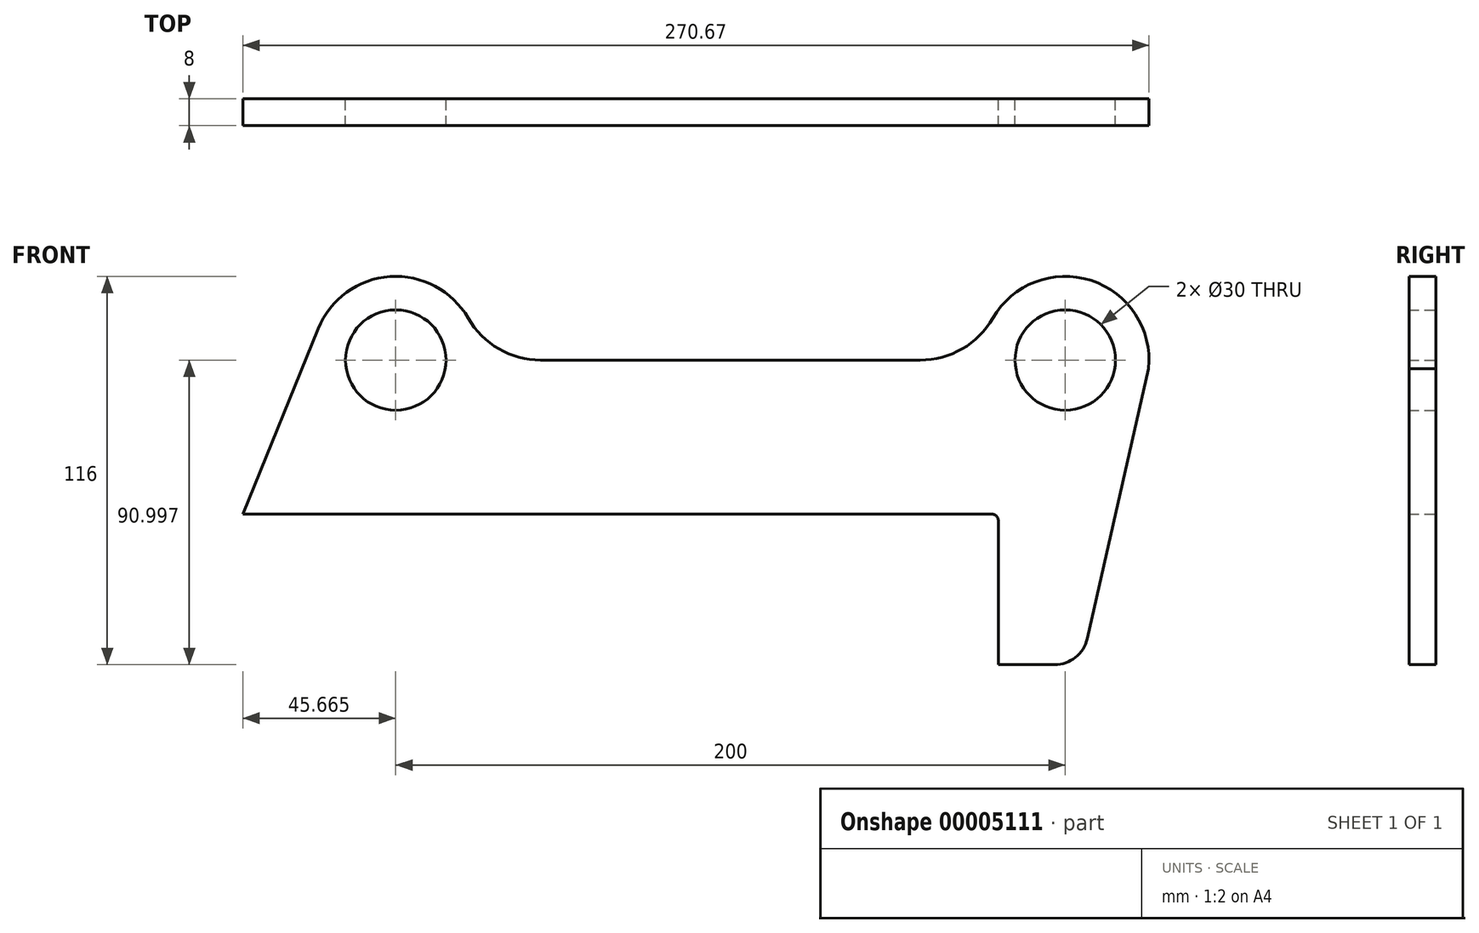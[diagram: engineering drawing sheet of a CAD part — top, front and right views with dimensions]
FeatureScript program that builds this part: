
annotation { "Feature Type Name" : "Feature", "Feature Type Description" : "" }
export const myFeature = defineFeature(function(context is Context, id is Id, definition is map)
    precondition{}
    {
        {
            var Q0;
            Q0=qCreatedBy(makeId("Front.planeOp"),FACE);
            var sketch = newSketch(context, id + "F0", { "sketchPlane" : qUnion([Q0])});
            skCircle(sketch, "E0", {"center": v(-194.03, 41.42) * mm, "radius": 15 * mm});
            skCircle(sketch, "E1", {"center": v(5.97, 41.42) * mm, "radius": 15 * mm});
            skArc(sketch, "E2", {"start": v(-172.38, 53.92) * mm, "mid": v(-195.76, 66.36) * mm, "end": v(-217.2, 50.82) * mm});
            skArc(sketch, "E3", {"start": v(30.84, 38.89) * mm, "mid": v(13.65, 65.2) * mm, "end": v(-15.69, 53.92) * mm});
            skLineSegment(sketch, "E4", {"start": v(-150.73, 41.42) * mm, "end": v(-37.34, 41.42) * mm});
            skLineSegment(sketch, "E5.0", {"start": v(-239.7, -4.58) * mm, "end": v(-16.03, -4.58) * mm});
            skLineSegment(sketch, "E6.trimOffspring", {"start": v(-14.03, -6.58) * mm, "end": v(-14.03, -49.58) * mm});
            skLineSegment(sketch, "E7", {"start": v(-14.03, -49.58) * mm, "end": v(2.77, -49.58) * mm});
            skLineSegment(sketch, "E8", {"start": v(12.52, -41.8) * mm, "end": v(30.84, 38.89) * mm});
            skLineSegment(sketch, "E9", {"start": v(-239.7, -4.58) * mm, "end": v(-217.2, 50.82) * mm});
            skPoint(sketch, "E10.visualSharp", {"position": v(-169.03, 41.42) * mm});
            skArc(sketch, "E10.filletArc", {"start": v(-172.38, 53.92) * mm, "mid": v(-163.23, 44.77) * mm, "end": v(-150.73, 41.42) * mm});
            skPoint(sketch, "E11.visualSharp", {"position": v(-19.03, 41.42) * mm});
            skArc(sketch, "E11.filletArc", {"start": v(-37.34, 41.42) * mm, "mid": v(-24.84, 44.77) * mm, "end": v(-15.69, 53.92) * mm});
            skPoint(sketch, "E12.visualSharp", {"position": v(-14.03, -4.58) * mm});
            skArc(sketch, "E12.filletArc", {"start": v(-14.03, -6.58) * mm, "mid": v(-14.62, -5.17) * mm, "end": v(-16.03, -4.58) * mm});
            skPoint(sketch, "E13.visualSharp", {"position": v(10.75, -49.58) * mm});
            skArc(sketch, "E13.filletArc", {"start": v(2.77, -49.58) * mm, "mid": v(9, -47.4) * mm, "end": v(12.52, -41.8) * mm});
            skSolve(sketch);
        }
        {
            var Q0;
            Q0=makeQuery(id+"F0.imprint","IMPRINT",FACE,{"disambiguationData":[TD([[makeQuery(id+"F0.imprint","IMPRINT",EDGE,{"derivedFrom":sQuery(id+"F0.wireOp",EDGE,"E0")}),-1.0]])]});
            extrude(context, id + "F1", {"entities" : qUnion([Q0]), "depth" : 8 * mm});
        }
    });
